# Revit family: Commercial_Shower_System-American_Standard-TU662223.002
name_source: partatom
category: Plumbing Fixtures
units: mm (PartAtom-declared; Revit-internal decimal feet)

## family parameters
Cut with Voids When Loaded = No
Host = Face
OmniClass Number = 23.45.05.14.17
OmniClass Title = Showers
Part Type = Normal
Room Calculation Point = No
Round Connector Dimension = Use Diameter
Shared = Yes

## types (1)
- TU662223.002
    ADA Compliant = Yes
    Assembly Code = D2010710
    CW Connection = Yes
    CWFU = 3
    Cold Water Connection Description = 1/2" NPT Female CW Inlet Connection
    Cold Water Connection Diameter = 1/2"
    Cold Water Connection Radius = 1/4"
    Default Elevation = 0"
    Description = Commercial Shower System Trim Kit 2.5 gpm/9.5 Lpm With 36-Inch Slide Bar, Hand Shower and Showerhead
    Diverter Trim Kit Height = 48"
    Diverter Trim Kit Width = 8"
    Finish = Metal-American Standard-002-Polished Chrome
    Flow Rate = 2.5 gpf/9.5 Lpm
    HW Connection = Yes
    HWFU = 3
    Height = 78"
    Hot Water Connection Description = 1/2" NPT Female HW Inlet Connection
    Hot Water Connection Diameter = 1/2"
    Hot Water Connection Radius = 1/4"
    IAPMO Compliance = These products meets or exceeds ASSE 1016AS ME A112 .18 .1016CSA B12 5 .16AS ME A112 .18 .1CSA B12 5 .1
    Installation Type = Wall Mounted
    Manufacturer = American Standard
    Material = Metal-American Standard-Polished Chrome
    Model = TU662223.002
    Outlet Connection Description = 1/2" NPS Male Outlet Connection
    Price = Prices may vary. Please consult Manufacturer Representative for most up-to-date price list.
    Product Documentation Link = https://americanstandard.box.com
    Product Page URL = https://www.americanstandard-us.com
    Showerhead Height = 78"
    Showerhead Width = 8"
    Slide Bar Height = 50"
    Type Comments = Flash rough-in valve and 2-way diverter valve (R422) must be purchased separately
    URL = https://www.americanstandard-us.com
    Valve Trim Height = 45"
    Valve Trim Width = 8"
    Vent Connection = No
    WFU = 4
    Warranty Documentation Link = https://www.americanstandard-us.com
    Waste Connection = No

## geometry (parser evidence)
native form markers: Sweep x30
no freeform markers — native parametric forms only
